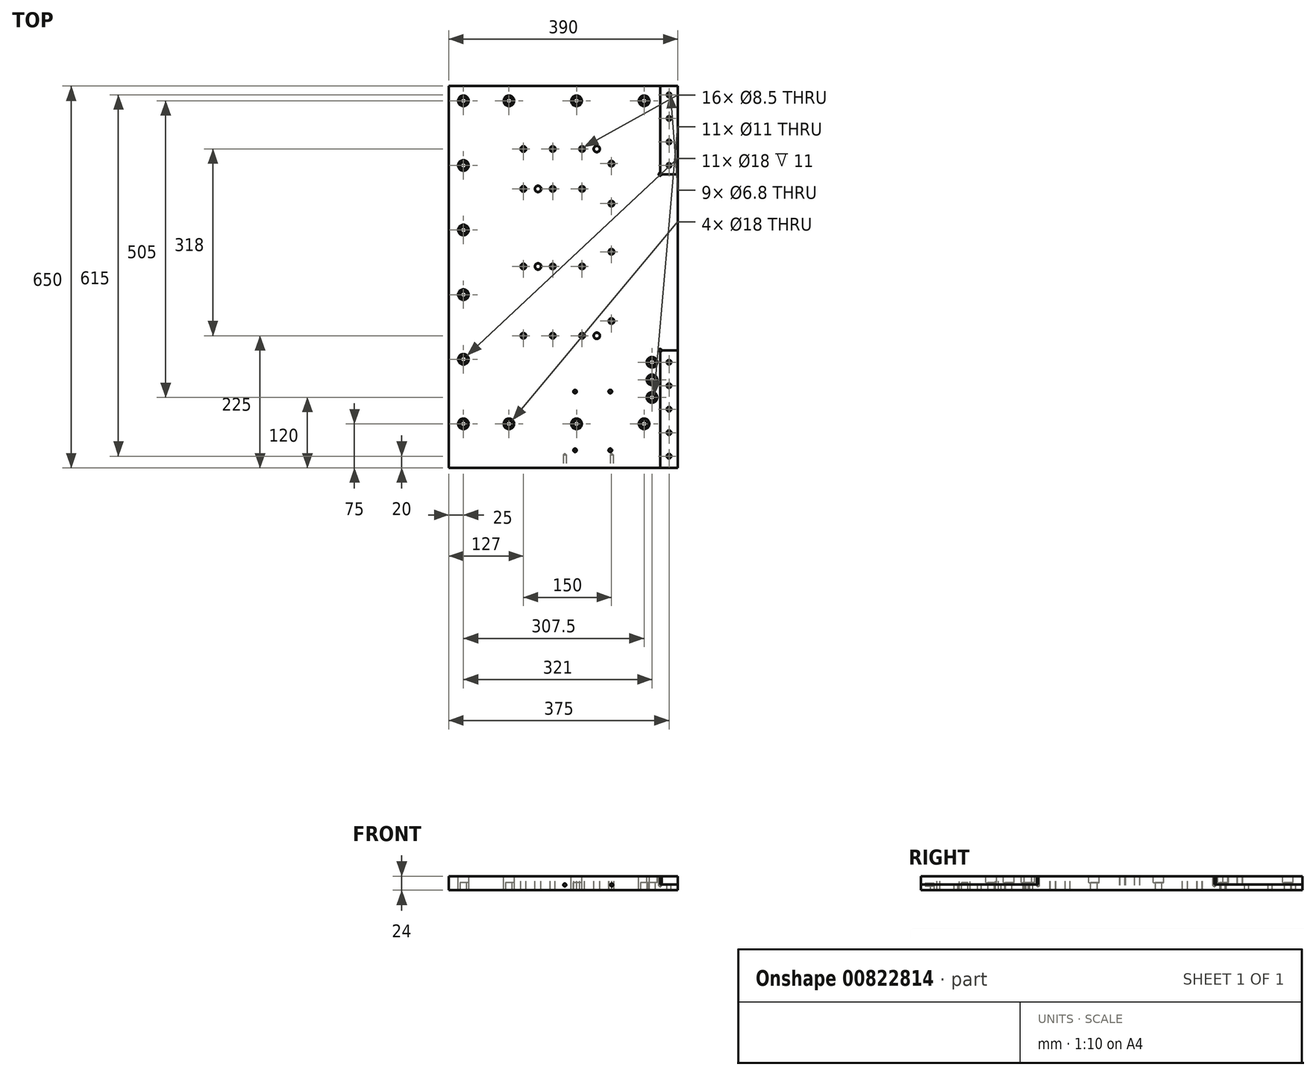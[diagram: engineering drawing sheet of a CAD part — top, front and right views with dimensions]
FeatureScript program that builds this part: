
annotation { "Feature Type Name" : "Feature", "Feature Type Description" : "" }
export const myFeature = defineFeature(function(context is Context, id is Id, definition is map)
    precondition{}
    {
        {
            var Q0;
            Q0=qCreatedBy(makeId("Top.planeOp"),FACE);
            var sketch = newSketch(context, id + "F0", { "sketchPlane" : qUnion([Q0])});
            skLineSegment(sketch, "E0.bottom", {"start": v(-195, -325) * mm, "end": v(195, -325) * mm});
            skLineSegment(sketch, "E0.top", {"start": v(-195, 325) * mm, "end": v(195, 325) * mm});
            skLineSegment(sketch, "E0.left", {"start": v(-195, -325) * mm, "end": v(-195, 325) * mm});
            skLineSegment(sketch, "E0.right", {"start": v(195, -325) * mm, "end": v(195, 325) * mm});
            skPoint(sketch, "E0.middle", {"position": v(0, 0) * mm});
            skSolve(sketch);
        }
        {
            var Q0;
            Q0 = qSketchRegion(id + "F0", true);
            extrude(context, id + "F1", {"entities" : qUnion([Q0]), "depth" : 24 * mm, "offsetDistance" : 25 * mm});
        }
        {
            var Q0;
            Q0=makeQuery(id+"F1.opExtrude","CAP_FACE",FACE,{"disambiguationData":[OSD([sQuery(id+"F0.wireOp",EDGE,"E0.bottom"),sQuery(id+"F0.wireOp",EDGE,"E0.top"),sQuery(id+"F0.wireOp",EDGE,"E0.left"),sQuery(id+"F0.wireOp",EDGE,"E0.right")])],"isStart":false});
            var sketch = newSketch(context, id + "F2", { "sketchPlane" : qUnion([Q0])});
            skLineSegment(sketch, "E1.0.0", {"start": v(195, 325) * mm, "end": v(-195, 325) * mm, "construction": true});
            skLineSegment(sketch, "E1.0.1", {"start": v(-195, 325) * mm, "end": v(-195, -325) * mm, "construction": true});
            skLineSegment(sketch, "E1.0.2", {"start": v(-195, -325) * mm, "end": v(195, -325) * mm, "construction": true});
            skLineSegment(sketch, "E1.0.3", {"start": v(195, -325) * mm, "end": v(195, 325) * mm, "construction": true});
            skLineSegment(sketch, "E2", {"start": v(195, -125) * mm, "end": v(165, -125) * mm, "construction": true});
            skLineSegment(sketch, "E3", {"start": v(165, -125) * mm, "end": v(165, -325) * mm, "construction": true});
            skLineSegment(sketch, "E4", {"start": v(195, 175) * mm, "end": v(165, 175) * mm, "construction": true});
            skLineSegment(sketch, "E5", {"start": v(165, 175) * mm, "end": v(165, 325) * mm, "construction": true});
            skLineSegment(sketch, "E6.bottom", {"start": v(165, 175) * mm, "end": v(195, 175) * mm});
            skLineSegment(sketch, "E6.top", {"start": v(165, 325) * mm, "end": v(195, 325) * mm});
            skLineSegment(sketch, "E6.left", {"start": v(165, 175) * mm, "end": v(165, 325) * mm});
            skLineSegment(sketch, "E6.right", {"start": v(195, 175) * mm, "end": v(195, 325) * mm});
            skLineSegment(sketch, "E7.bottom", {"start": v(165, -125) * mm, "end": v(195, -125) * mm});
            skLineSegment(sketch, "E7.top", {"start": v(165, -325) * mm, "end": v(195, -325) * mm});
            skLineSegment(sketch, "E7.left", {"start": v(165, -125) * mm, "end": v(165, -325) * mm});
            skLineSegment(sketch, "E7.right", {"start": v(195, -125) * mm, "end": v(195, -325) * mm});
            skSolve(sketch);
        }
        {
            var Q0;
            {var subQ3=sQuery(id+"F2.wireOp",EDGE,"E6.bottom");Q0=makeQuery(id+"F2.imprint","IMPRINT",FACE,{"disambiguationData":[TD([[makeQuery(id+"F2.imprint","IMPRINT",EDGE,{"derivedFrom":subQ3}),-1.0]])]});}
            var sketch = newSketch(context, id + "F3", { "sketchPlane" : qUnion([Q0])});
            skLineSegment(sketch, "E8.0", {"start": v(165, 175) * mm, "end": v(165, 325) * mm, "construction": true});
            skLineSegment(sketch, "E9.0", {"start": v(165, 175) * mm, "end": v(195, 175) * mm, "construction": true});
            skLineSegment(sketch, "E10.0", {"start": v(165, -125) * mm, "end": v(195, -125) * mm, "construction": true});
            skLineSegment(sketch, "E11.0", {"start": v(165, -125) * mm, "end": v(165, -325) * mm, "construction": true});
            skCircle(sketch, "E12", {"center": v(165, 175) * mm, "radius": 2.5 * mm});
            skCircle(sketch, "E13", {"center": v(165, -125) * mm, "radius": 2.5 * mm});
            skSolve(sketch);
        }
        {
            var Q0;
            Q0 = qSketchRegion(id + "F2", true);
            extrude(context, id + "F4", {"entities" : qUnion([Q0]), "operationType" : NewBodyOperationType.REMOVE, "oppositeDirection" : true, "depth" : 14 * mm, "offsetDistance" : 25 * mm});
        }
        {
            var Q0;
            Q0 = qSketchRegion(id + "F3", true);
            extrude(context, id + "F5", {"entities" : qUnion([Q0]), "operationType" : NewBodyOperationType.REMOVE, "oppositeDirection" : true, "depth" : (16 + 2.5) * mm, "offsetDistance" : 25 * mm});
        }
        {
            var Q0;
            Q0=makeQuery(id+"F5.boolean.opBoolean","COPY",FACE,{"derivedFrom":makeQuery(id+"F5.opExtrude","CAP_FACE",FACE,{"disambiguationData":[OSD([sQuery(id+"F3.wireOp",EDGE,"E13")])],"isStart":false})});
            var Q1;
            Q1=makeQuery(id+"F5.boolean.opBoolean","COPY",FACE,{"derivedFrom":makeQuery(id+"F5.opExtrude","CAP_FACE",FACE,{"disambiguationData":[OSD([sQuery(id+"F3.wireOp",EDGE,"E12")])],"isStart":false})});
            chamfer(context, id + "F6", {"entities" : qUnion([Q0, Q1]), "width" : 2.5 * mm, "tangentPropagation" : true});
        }
        {
            var Q0;
            Q0=makeQuery(id+"F1.opExtrude","CAP_FACE",FACE,{"disambiguationData":[OSD([sQuery(id+"F0.wireOp",EDGE,"E0.bottom"),sQuery(id+"F0.wireOp",EDGE,"E0.top"),sQuery(id+"F0.wireOp",EDGE,"E0.left"),sQuery(id+"F0.wireOp",EDGE,"E0.right")])],"isStart":false});
            var sketch = newSketch(context, id + "F7", { "sketchPlane" : qUnion([Q0])});
            skLineSegment(sketch, "E14.bottom", {"start": v(479.08, -265.8) * mm, "end": v(-298.76, -265.8) * mm, "construction": true});
            skLineSegment(sketch, "E14.top", {"start": v(479.08, -215) * mm, "end": v(-298.76, -215) * mm, "construction": true});
            skLineSegment(sketch, "E14.left", {"start": v(479.08, -265.8) * mm, "end": v(479.08, -215) * mm, "construction": true});
            skLineSegment(sketch, "E14.right", {"start": v(-298.76, -265.8) * mm, "end": v(-298.76, -215) * mm, "construction": true});
            skLineSegment(sketch, "E15.bottom", {"start": v(-285.1, 315.8) * mm, "end": v(454.5, 315.8) * mm, "construction": true});
            skLineSegment(sketch, "E15.top", {"start": v(-285.1, 265) * mm, "end": v(454.5, 265) * mm, "construction": true});
            skLineSegment(sketch, "E15.left", {"start": v(-285.1, 315.8) * mm, "end": v(-285.1, 265) * mm, "construction": true});
            skLineSegment(sketch, "E15.right", {"start": v(454.5, 315.8) * mm, "end": v(454.5, 265) * mm, "construction": true});
            skArc(sketch, "E16.0.0", {"start": v(167.5, 175) * mm, "mid": v(163.23, 173.23) * mm, "end": v(165, 177.5) * mm, "construction": true});
            skLineSegment(sketch, "E16.0.1", {"start": v(165, 177.5) * mm, "end": v(165, 325) * mm, "construction": true});
            skLineSegment(sketch, "E16.0.2", {"start": v(165, 325) * mm, "end": v(-195, 325) * mm, "construction": true});
            skLineSegment(sketch, "E16.0.3", {"start": v(-195, 325) * mm, "end": v(-195, -325) * mm, "construction": true});
            skLineSegment(sketch, "E16.0.4", {"start": v(-195, -325) * mm, "end": v(165, -325) * mm, "construction": true});
            skLineSegment(sketch, "E16.0.5", {"start": v(165, -325) * mm, "end": v(165, -127.5) * mm, "construction": true});
            skArc(sketch, "E16.0.6", {"start": v(165, -127.5) * mm, "mid": v(163.23, -123.23) * mm, "end": v(167.5, -125) * mm, "construction": true});
            skLineSegment(sketch, "E16.0.7", {"start": v(167.5, -125) * mm, "end": v(195, -125) * mm, "construction": true});
            skLineSegment(sketch, "E16.0.8", {"start": v(195, -125) * mm, "end": v(195, 175) * mm, "construction": true});
            skLineSegment(sketch, "E16.0.9", {"start": v(195, 175) * mm, "end": v(167.5, 175) * mm, "construction": true});
            skArc(sketch, "E17.0.0", {"start": v(165, 202.5) * mm, "mid": v(192.5, 202.5) * mm, "end": v(192.5, 175) * mm, "construction": true});
            skLineSegment(sketch, "E17.0.1", {"start": v(192.5, 175) * mm, "end": v(195, 175) * mm, "construction": true});
            skLineSegment(sketch, "E17.0.2", {"start": v(195, 175) * mm, "end": v(195, 325) * mm, "construction": true});
            skLineSegment(sketch, "E17.0.3", {"start": v(195, 325) * mm, "end": v(165, 325) * mm, "construction": true});
            skLineSegment(sketch, "E17.0.4", {"start": v(165, 325) * mm, "end": v(165, 202.5) * mm, "construction": true});
            skArc(sketch, "E18.0.0", {"start": v(192.5, -125) * mm, "mid": v(167.5, -127.5) * mm, "end": v(165, -102.5) * mm, "construction": true});
            skLineSegment(sketch, "E18.0.1", {"start": v(165, -102.5) * mm, "end": v(165, -325) * mm, "construction": true});
            skLineSegment(sketch, "E18.0.2", {"start": v(165, -325) * mm, "end": v(195, -325) * mm, "construction": true});
            skLineSegment(sketch, "E18.0.3", {"start": v(195, -325) * mm, "end": v(195, -125) * mm, "construction": true});
            skLineSegment(sketch, "E18.0.4", {"start": v(195, -125) * mm, "end": v(192.5, -125) * mm, "construction": true});
            skPoint(sketch, "E19.endSnap0", {"position": v(181.25, 175) * mm});
            skLineSegment(sketch, "E20", {"start": v(180, -325) * mm, "end": v(180, 325) * mm, "construction": true});
            skCircle(sketch, "E21", {"center": v(180, 310) * mm, "radius": 3.4 * mm});
            skCircle(sketch, "E22", {"center": v(180, 230) * mm, "radius": 3.4 * mm});
            skCircle(sketch, "E23", {"center": v(180, 190) * mm, "radius": 3.4 * mm});
            skCircle(sketch, "E24", {"center": v(180, -145) * mm, "radius": 3.4 * mm});
            skCircle(sketch, "E25", {"center": v(180, -185) * mm, "radius": 3.4 * mm});
            skCircle(sketch, "E26", {"center": v(180, -225) * mm, "radius": 3.4 * mm});
            skCircle(sketch, "E27", {"center": v(180, -265) * mm, "radius": 3.4 * mm});
            skCircle(sketch, "E28", {"center": v(180, -305) * mm, "radius": 3.4 * mm});
            skCircle(sketch, "E29", {"center": v(180, 270) * mm, "radius": 3.4 * mm});
            skCircle(sketch, "E30", {"center": v(180, -345) * mm, "radius": 3.4 * mm, "construction": true});
            skSolve(sketch);
        }
        {
            var Q0;
            Q0 = qSketchRegion(id + "F7", true);
            extrude(context, id + "F8", {"entities" : qUnion([Q0]), "operationType" : NewBodyOperationType.REMOVE, "oppositeDirection" : true, "depth" : 25 * mm, "offsetDistance" : 25 * mm});
        }
        {
            var Q0;
            Q0=makeQuery(id+"F8.boolean.opBoolean","COPY",FACE,{"derivedFrom":makeQuery(id+"F8.opExtrude","SWEPT_FACE",FACE,{"disambiguationData":[OSD([sQuery(id+"F7.wireOp",EDGE,"E28")])]})});
            var Q1;
            Q1=makeQuery(id+"F8.boolean.opBoolean","COPY",FACE,{"derivedFrom":makeQuery(id+"F8.opExtrude","SWEPT_FACE",FACE,{"disambiguationData":[OSD([sQuery(id+"F7.wireOp",EDGE,"E27")])]})});
            var Q2;
            Q2=makeQuery(id+"F8.boolean.opBoolean","COPY",FACE,{"derivedFrom":makeQuery(id+"F8.opExtrude","SWEPT_FACE",FACE,{"disambiguationData":[OSD([sQuery(id+"F7.wireOp",EDGE,"E26")])]})});
            var Q3;
            Q3=makeQuery(id+"F8.boolean.opBoolean","COPY",FACE,{"derivedFrom":makeQuery(id+"F8.opExtrude","SWEPT_FACE",FACE,{"disambiguationData":[OSD([sQuery(id+"F7.wireOp",EDGE,"E25")])]})});
            var Q4;
            Q4=makeQuery(id+"F8.boolean.opBoolean","COPY",FACE,{"derivedFrom":makeQuery(id+"F8.opExtrude","SWEPT_FACE",FACE,{"disambiguationData":[OSD([sQuery(id+"F7.wireOp",EDGE,"E24")])]})});
            var Q5;
            Q5=makeQuery(id+"F8.boolean.opBoolean","COPY",FACE,{"derivedFrom":makeQuery(id+"F8.opExtrude","SWEPT_FACE",FACE,{"disambiguationData":[OSD([sQuery(id+"F7.wireOp",EDGE,"E23")])]})});
            var Q6;
            Q6=makeQuery(id+"F8.boolean.opBoolean","COPY",FACE,{"derivedFrom":makeQuery(id+"F8.opExtrude","SWEPT_FACE",FACE,{"disambiguationData":[OSD([sQuery(id+"F7.wireOp",EDGE,"E22")])]})});
            var Q7;
            Q7=makeQuery(id+"F8.boolean.opBoolean","COPY",FACE,{"derivedFrom":makeQuery(id+"F8.opExtrude","SWEPT_FACE",FACE,{"disambiguationData":[OSD([sQuery(id+"F7.wireOp",EDGE,"E29")])]})});
            var Q8;
            Q8=makeQuery(id+"F8.boolean.opBoolean","COPY",FACE,{"derivedFrom":makeQuery(id+"F8.opExtrude","SWEPT_FACE",FACE,{"disambiguationData":[OSD([sQuery(id+"F7.wireOp",EDGE,"E21")])]})});
            chamfer(context, id + "F9", {"entities" : qUnion([Q0, Q1, Q2, Q3, Q4, Q5, Q6, Q7, Q8]), "width" : 0.5 * mm, "tangentPropagation" : true});
        }
        {
            var Q0;
            Q0=makeQuery(id+"F1.opExtrude","CAP_FACE",FACE,{"disambiguationData":[OSD([sQuery(id+"F0.wireOp",EDGE,"E0.bottom"),sQuery(id+"F0.wireOp",EDGE,"E0.top"),sQuery(id+"F0.wireOp",EDGE,"E0.left"),sQuery(id+"F0.wireOp",EDGE,"E0.right")])],"isStart":false});
            var sketch = newSketch(context, id + "F10", { "sketchPlane" : qUnion([Q0])});
            skLineSegment(sketch, "E31.0", {"start": v(-195, -325) * mm, "end": v(-195, 325) * mm, "construction": true});
            skLineSegment(sketch, "E32.0", {"start": v(-195, 325) * mm, "end": v(165, 325) * mm, "construction": true});
            skLineSegment(sketch, "E33.0", {"start": v(195, -125) * mm, "end": v(195, 175) * mm, "construction": true});
            skLineSegment(sketch, "E34", {"start": v(-353.17, 300) * mm, "end": v(198.25, 300) * mm, "construction": true});
            skCircle(sketch, "E35", {"center": v(137.5, 300) * mm, "radius": 5.5 * mm});
            skCircle(sketch, "E36.1.0.0", {"center": v(22.5, 300) * mm, "radius": 5.5 * mm});
            skCircle(sketch, "E36.2.0.0", {"center": v(-92.5, 300) * mm, "radius": 5.5 * mm});
            skLineSegment(sketch, "E36.direction1", {"start": v(137.5, 300) * mm, "end": v(22.5, 300) * mm, "construction": true});
            skCircle(sketch, "E37.0.3.0", {"center": v(-207.5, 300) * mm, "radius": 5.5 * mm, "construction": true});
            skLineSegment(sketch, "E38", {"start": v(-117.5, 418.15) * mm, "end": v(-117.5, -388.99) * mm, "construction": true});
            skLineSegment(sketch, "E39", {"start": v(-67.5, 418.15) * mm, "end": v(-67.5, -388.99) * mm, "construction": true});
            skLineSegment(sketch, "E40", {"start": v(195, 25) * mm, "end": v(452.46, 25) * mm, "construction": true});
            skCircle(sketch, "E41.MirrorC", {"center": v(22.5, -250) * mm, "radius": 5.5 * mm});
            skCircle(sketch, "E42.MirrorC", {"center": v(137.5, -250) * mm, "radius": 5.5 * mm});
            skCircle(sketch, "E43.MirrorC", {"center": v(-92.5, -250) * mm, "radius": 5.5 * mm});
            skCircle(sketch, "E44", {"center": v(-170, 300) * mm, "radius": 5.5 * mm});
            skCircle(sketch, "E45.MirrorC", {"center": v(-170, -250) * mm, "radius": 5.5 * mm});
            skCircle(sketch, "E46.0.1.0", {"center": v(-170, 190) * mm, "radius": 5.5 * mm});
            skCircle(sketch, "E46.0.2.0", {"center": v(-170, 80) * mm, "radius": 5.5 * mm});
            skCircle(sketch, "E46.0.3.0", {"center": v(-170, -30) * mm, "radius": 5.5 * mm});
            skCircle(sketch, "E46.0.4.0", {"center": v(-170, -140) * mm, "radius": 5.5 * mm});
            skLineSegment(sketch, "E46.direction1", {"start": v(-170, 300) * mm, "end": v(-145, 300) * mm, "construction": true});
            skLineSegment(sketch, "E46.direction2", {"start": v(-170, 300) * mm, "end": v(-170, 190) * mm, "construction": true});
            skCircle(sketch, "E47", {"center": v(-170, 300) * mm, "radius": 9 * mm});
            skCircle(sketch, "E48", {"center": v(-92.5, 300) * mm, "radius": 9 * mm});
            skCircle(sketch, "E49.0.1.0", {"center": v(-170, 190) * mm, "radius": 9 * mm});
            skCircle(sketch, "E49.0.2.0", {"center": v(-170, 80) * mm, "radius": 9 * mm});
            skCircle(sketch, "E49.0.3.0", {"center": v(-170, -30) * mm, "radius": 9 * mm});
            skCircle(sketch, "E49.0.4.0", {"center": v(-170, -140) * mm, "radius": 9 * mm});
            skCircle(sketch, "E49.0.5.0", {"center": v(-170, -250) * mm, "radius": 9 * mm});
            skCircle(sketch, "E50.1.0.0", {"center": v(22.5, 300) * mm, "radius": 9 * mm});
            skCircle(sketch, "E50.2.0.0", {"center": v(137.5, 300) * mm, "radius": 9 * mm});
            skLineSegment(sketch, "E50.direction1", {"start": v(-92.5, 300) * mm, "end": v(22.5, 300) * mm, "construction": true});
            skCircle(sketch, "E51.MirrorC", {"center": v(22.5, -250) * mm, "radius": 9 * mm});
            skCircle(sketch, "E52.MirrorC", {"center": v(137.5, -250) * mm, "radius": 9 * mm});
            skCircle(sketch, "E53.MirrorC", {"center": v(-92.5, -250) * mm, "radius": 9 * mm});
            skSolve(sketch);
        }
        {
            var Q0;
            Q0=makeQuery(id+"F10.imprint","IMPRINT",FACE,{"disambiguationData":[TD([[makeQuery(id+"F10.imprint","IMPRINT",EDGE,{"derivedFrom":sQuery(id+"F10.wireOp",EDGE,"E35")}),1.0]])]});
            var Q1;
            Q1=makeQuery(id+"F10.imprint","IMPRINT",FACE,{"disambiguationData":[TD([[makeQuery(id+"F10.imprint","IMPRINT",EDGE,{"derivedFrom":sQuery(id+"F10.wireOp",EDGE,"E36.1.0.0")}),1.0]])]});
            var Q2;
            Q2=makeQuery(id+"F10.imprint","IMPRINT",FACE,{"disambiguationData":[TD([[makeQuery(id+"F10.imprint","IMPRINT",EDGE,{"derivedFrom":sQuery(id+"F10.wireOp",EDGE,"E36.2.0.0")}),1.0]])]});
            var Q3;
            Q3=makeQuery(id+"F10.imprint","IMPRINT",FACE,{"disambiguationData":[TD([[makeQuery(id+"F10.imprint","IMPRINT",EDGE,{"derivedFrom":sQuery(id+"F10.wireOp",EDGE,"E44")}),1.0]])]});
            var Q4;
            Q4=makeQuery(id+"F10.imprint","IMPRINT",FACE,{"disambiguationData":[TD([[makeQuery(id+"F10.imprint","IMPRINT",EDGE,{"derivedFrom":sQuery(id+"F10.wireOp",EDGE,"E46.0.1.0")}),1.0]])]});
            var Q5;
            Q5=makeQuery(id+"F10.imprint","IMPRINT",FACE,{"disambiguationData":[TD([[makeQuery(id+"F10.imprint","IMPRINT",EDGE,{"derivedFrom":sQuery(id+"F10.wireOp",EDGE,"E46.0.2.0")}),1.0]])]});
            var Q6;
            Q6=makeQuery(id+"F10.imprint","IMPRINT",FACE,{"disambiguationData":[TD([[makeQuery(id+"F10.imprint","IMPRINT",EDGE,{"derivedFrom":sQuery(id+"F10.wireOp",EDGE,"E46.0.3.0")}),1.0]])]});
            var Q7;
            Q7=makeQuery(id+"F10.imprint","IMPRINT",FACE,{"disambiguationData":[TD([[makeQuery(id+"F10.imprint","IMPRINT",EDGE,{"derivedFrom":sQuery(id+"F10.wireOp",EDGE,"E46.0.4.0")}),1.0]])]});
            var Q8;
            Q8=makeQuery(id+"F10.imprint","IMPRINT",FACE,{"disambiguationData":[TD([[makeQuery(id+"F10.imprint","IMPRINT",EDGE,{"derivedFrom":sQuery(id+"F10.wireOp",EDGE,"E45.MirrorC")}),-1.0]])]});
            var Q9;
            Q9=makeQuery(id+"F10.imprint","IMPRINT",FACE,{"disambiguationData":[TD([[makeQuery(id+"F10.imprint","IMPRINT",EDGE,{"derivedFrom":sQuery(id+"F10.wireOp",EDGE,"E43.MirrorC")}),-1.0]])]});
            var Q10;
            Q10=makeQuery(id+"F10.imprint","IMPRINT",FACE,{"disambiguationData":[TD([[makeQuery(id+"F10.imprint","IMPRINT",EDGE,{"derivedFrom":sQuery(id+"F10.wireOp",EDGE,"E41.MirrorC")}),-1.0]])]});
            var Q11;
            Q11=makeQuery(id+"F10.imprint","IMPRINT",FACE,{"disambiguationData":[TD([[makeQuery(id+"F10.imprint","IMPRINT",EDGE,{"derivedFrom":sQuery(id+"F10.wireOp",EDGE,"E42.MirrorC")}),-1.0]])]});
            extrude(context, id + "F11", {"entities" : qUnion([Q0, Q1, Q2, Q3, Q4, Q5, Q6, Q7, Q8, Q9, Q10, Q11]), "operationType" : NewBodyOperationType.REMOVE, "oppositeDirection" : true, "depth" : 25 * mm, "offsetDistance" : 25 * mm});
        }
        {
            var Q0;
            Q0=makeQuery(id+"F10.imprint","IMPRINT",FACE,{"disambiguationData":[TD([[makeQuery(id+"F10.imprint","IMPRINT",EDGE,{"derivedFrom":sQuery(id+"F10.wireOp",EDGE,"E35")}),-1.0]])]});
            var Q1;
            Q1=makeQuery(id+"F10.imprint","IMPRINT",FACE,{"disambiguationData":[TD([[makeQuery(id+"F10.imprint","IMPRINT",EDGE,{"derivedFrom":sQuery(id+"F10.wireOp",EDGE,"E36.1.0.0")}),-1.0]])]});
            var Q2;
            Q2=makeQuery(id+"F10.imprint","IMPRINT",FACE,{"disambiguationData":[TD([[makeQuery(id+"F10.imprint","IMPRINT",EDGE,{"derivedFrom":sQuery(id+"F10.wireOp",EDGE,"E36.2.0.0")}),-1.0]])]});
            var Q3;
            Q3=makeQuery(id+"F10.imprint","IMPRINT",FACE,{"disambiguationData":[TD([[makeQuery(id+"F10.imprint","IMPRINT",EDGE,{"derivedFrom":sQuery(id+"F10.wireOp",EDGE,"E44")}),-1.0]])]});
            var Q4;
            Q4=makeQuery(id+"F10.imprint","IMPRINT",FACE,{"disambiguationData":[TD([[makeQuery(id+"F10.imprint","IMPRINT",EDGE,{"derivedFrom":sQuery(id+"F10.wireOp",EDGE,"E46.0.1.0")}),-1.0]])]});
            var Q5;
            Q5=makeQuery(id+"F10.imprint","IMPRINT",FACE,{"disambiguationData":[TD([[makeQuery(id+"F10.imprint","IMPRINT",EDGE,{"derivedFrom":sQuery(id+"F10.wireOp",EDGE,"E46.0.2.0")}),-1.0]])]});
            var Q6;
            Q6=makeQuery(id+"F10.imprint","IMPRINT",FACE,{"disambiguationData":[TD([[makeQuery(id+"F10.imprint","IMPRINT",EDGE,{"derivedFrom":sQuery(id+"F10.wireOp",EDGE,"E46.0.3.0")}),-1.0]])]});
            var Q7;
            Q7=makeQuery(id+"F10.imprint","IMPRINT",FACE,{"disambiguationData":[TD([[makeQuery(id+"F10.imprint","IMPRINT",EDGE,{"derivedFrom":sQuery(id+"F10.wireOp",EDGE,"E46.0.4.0")}),-1.0]])]});
            var Q8;
            Q8=makeQuery(id+"F10.imprint","IMPRINT",FACE,{"disambiguationData":[TD([[makeQuery(id+"F10.imprint","IMPRINT",EDGE,{"derivedFrom":sQuery(id+"F10.wireOp",EDGE,"E45.MirrorC")}),1.0]])]});
            var Q9;
            Q9=makeQuery(id+"F10.imprint","IMPRINT",FACE,{"disambiguationData":[TD([[makeQuery(id+"F10.imprint","IMPRINT",EDGE,{"derivedFrom":sQuery(id+"F10.wireOp",EDGE,"E43.MirrorC")}),1.0]])]});
            var Q10;
            Q10=makeQuery(id+"F10.imprint","IMPRINT",FACE,{"disambiguationData":[TD([[makeQuery(id+"F10.imprint","IMPRINT",EDGE,{"derivedFrom":sQuery(id+"F10.wireOp",EDGE,"E41.MirrorC")}),1.0]])]});
            var Q11;
            Q11=makeQuery(id+"F10.imprint","IMPRINT",FACE,{"disambiguationData":[TD([[makeQuery(id+"F10.imprint","IMPRINT",EDGE,{"derivedFrom":sQuery(id+"F10.wireOp",EDGE,"E42.MirrorC")}),1.0]])]});
            extrude(context, id + "F12", {"entities" : qUnion([Q0, Q1, Q2, Q3, Q4, Q5, Q6, Q7, Q8, Q9, Q10, Q11]), "operationType" : NewBodyOperationType.REMOVE, "oppositeDirection" : true, "depth" : 11 * mm, "offsetDistance" : 25 * mm});
        }
        {
            var Q0;
            Q0=makeQuery(id+"F12.boolean.opBoolean","COPY",EDGE,{"derivedFrom":makeQuery(id+"F12.opExtrude","CAP_EDGE",EDGE,{"disambiguationData":[OSD([sQuery(id+"F10.wireOp",EDGE,"E47")])],"isStart":true})});
            var Q1;
            Q1=makeQuery(id+"F12.boolean.opBoolean","COPY",EDGE,{"derivedFrom":makeQuery(id+"F12.opExtrude","CAP_EDGE",EDGE,{"disambiguationData":[OSD([sQuery(id+"F10.wireOp",EDGE,"E50.1.0.0")])],"isStart":true})});
            var Q2;
            Q2=makeQuery(id+"F12.boolean.opBoolean","COPY",EDGE,{"derivedFrom":makeQuery(id+"F12.opExtrude","CAP_EDGE",EDGE,{"disambiguationData":[OSD([sQuery(id+"F10.wireOp",EDGE,"E50.2.0.0")])],"isStart":true})});
            var Q3;
            Q3=makeQuery(id+"F12.boolean.opBoolean","COPY",EDGE,{"derivedFrom":makeQuery(id+"F12.opExtrude","CAP_EDGE",EDGE,{"disambiguationData":[OSD([sQuery(id+"F10.wireOp",EDGE,"E48")])],"isStart":true})});
            var Q4;
            Q4=makeQuery(id+"F12.boolean.opBoolean","COPY",EDGE,{"derivedFrom":makeQuery(id+"F12.opExtrude","CAP_EDGE",EDGE,{"disambiguationData":[OSD([sQuery(id+"F10.wireOp",EDGE,"E49.0.1.0")])],"isStart":true})});
            var Q5;
            Q5=makeQuery(id+"F12.boolean.opBoolean","COPY",EDGE,{"derivedFrom":makeQuery(id+"F12.opExtrude","CAP_EDGE",EDGE,{"disambiguationData":[OSD([sQuery(id+"F10.wireOp",EDGE,"E49.0.2.0")])],"isStart":true})});
            var Q6;
            Q6=makeQuery(id+"F12.boolean.opBoolean","COPY",EDGE,{"derivedFrom":makeQuery(id+"F12.opExtrude","CAP_EDGE",EDGE,{"disambiguationData":[OSD([sQuery(id+"F10.wireOp",EDGE,"E52.MirrorC")])],"isStart":true})});
            var Q7;
            Q7=makeQuery(id+"F12.boolean.opBoolean","COPY",EDGE,{"derivedFrom":makeQuery(id+"F12.opExtrude","CAP_EDGE",EDGE,{"disambiguationData":[OSD([sQuery(id+"F10.wireOp",EDGE,"E51.MirrorC")])],"isStart":true})});
            var Q8;
            Q8=makeQuery(id+"F12.boolean.opBoolean","COPY",EDGE,{"derivedFrom":makeQuery(id+"F12.opExtrude","CAP_EDGE",EDGE,{"disambiguationData":[OSD([sQuery(id+"F10.wireOp",EDGE,"E49.0.3.0")])],"isStart":true})});
            var Q9;
            Q9=makeQuery(id+"F12.boolean.opBoolean","COPY",EDGE,{"derivedFrom":makeQuery(id+"F12.opExtrude","CAP_EDGE",EDGE,{"disambiguationData":[OSD([sQuery(id+"F10.wireOp",EDGE,"E49.0.4.0")])],"isStart":true})});
            var Q10;
            Q10=makeQuery(id+"F12.boolean.opBoolean","COPY",EDGE,{"derivedFrom":makeQuery(id+"F12.opExtrude","CAP_EDGE",EDGE,{"disambiguationData":[OSD([sQuery(id+"F10.wireOp",EDGE,"E49.0.5.0")])],"isStart":true})});
            var Q11;
            Q11=makeQuery(id+"F12.boolean.opBoolean","COPY",EDGE,{"derivedFrom":makeQuery(id+"F12.opExtrude","CAP_EDGE",EDGE,{"disambiguationData":[OSD([sQuery(id+"F10.wireOp",EDGE,"E53.MirrorC")])],"isStart":true})});
            var Q12;
            Q12=makeQuery(id+"F11.boolean.opBoolean","INTERSECT",EDGE,{"derivedFrom":[makeQuery(id+"F1.opExtrude","CAP_FACE",FACE,{"disambiguationData":[OSD([sQuery(id+"F0.wireOp",EDGE,"E0.bottom"),sQuery(id+"F0.wireOp",EDGE,"E0.top"),sQuery(id+"F0.wireOp",EDGE,"E0.left"),sQuery(id+"F0.wireOp",EDGE,"E0.right")])],"isStart":true}),makeQuery(id+"F11.opExtrude","SWEPT_FACE",FACE,{"disambiguationData":[OSD([sQuery(id+"F10.wireOp",EDGE,"E42.MirrorC")])]})]});
            var Q13;
            Q13=makeQuery(id+"F11.boolean.opBoolean","INTERSECT",EDGE,{"derivedFrom":[makeQuery(id+"F1.opExtrude","CAP_FACE",FACE,{"disambiguationData":[OSD([sQuery(id+"F0.wireOp",EDGE,"E0.bottom"),sQuery(id+"F0.wireOp",EDGE,"E0.top"),sQuery(id+"F0.wireOp",EDGE,"E0.left"),sQuery(id+"F0.wireOp",EDGE,"E0.right")])],"isStart":true}),makeQuery(id+"F11.opExtrude","SWEPT_FACE",FACE,{"disambiguationData":[OSD([sQuery(id+"F10.wireOp",EDGE,"E41.MirrorC")])]})]});
            var Q14;
            Q14=makeQuery(id+"F11.boolean.opBoolean","INTERSECT",EDGE,{"derivedFrom":[makeQuery(id+"F1.opExtrude","CAP_FACE",FACE,{"disambiguationData":[OSD([sQuery(id+"F0.wireOp",EDGE,"E0.bottom"),sQuery(id+"F0.wireOp",EDGE,"E0.top"),sQuery(id+"F0.wireOp",EDGE,"E0.left"),sQuery(id+"F0.wireOp",EDGE,"E0.right")])],"isStart":true}),makeQuery(id+"F11.opExtrude","SWEPT_FACE",FACE,{"disambiguationData":[OSD([sQuery(id+"F10.wireOp",EDGE,"E43.MirrorC")])]})]});
            var Q15;
            Q15=makeQuery(id+"F11.boolean.opBoolean","INTERSECT",EDGE,{"derivedFrom":[makeQuery(id+"F1.opExtrude","CAP_FACE",FACE,{"disambiguationData":[OSD([sQuery(id+"F0.wireOp",EDGE,"E0.bottom"),sQuery(id+"F0.wireOp",EDGE,"E0.top"),sQuery(id+"F0.wireOp",EDGE,"E0.left"),sQuery(id+"F0.wireOp",EDGE,"E0.right")])],"isStart":true}),makeQuery(id+"F11.opExtrude","SWEPT_FACE",FACE,{"disambiguationData":[OSD([sQuery(id+"F10.wireOp",EDGE,"E45.MirrorC")])]})]});
            var Q16;
            Q16=makeQuery(id+"F11.boolean.opBoolean","INTERSECT",EDGE,{"derivedFrom":[makeQuery(id+"F1.opExtrude","CAP_FACE",FACE,{"disambiguationData":[OSD([sQuery(id+"F0.wireOp",EDGE,"E0.bottom"),sQuery(id+"F0.wireOp",EDGE,"E0.top"),sQuery(id+"F0.wireOp",EDGE,"E0.left"),sQuery(id+"F0.wireOp",EDGE,"E0.right")])],"isStart":true}),makeQuery(id+"F11.opExtrude","SWEPT_FACE",FACE,{"disambiguationData":[OSD([sQuery(id+"F10.wireOp",EDGE,"E46.0.4.0")])]})]});
            var Q17;
            Q17=makeQuery(id+"F11.boolean.opBoolean","INTERSECT",EDGE,{"derivedFrom":[makeQuery(id+"F1.opExtrude","CAP_FACE",FACE,{"disambiguationData":[OSD([sQuery(id+"F0.wireOp",EDGE,"E0.bottom"),sQuery(id+"F0.wireOp",EDGE,"E0.top"),sQuery(id+"F0.wireOp",EDGE,"E0.left"),sQuery(id+"F0.wireOp",EDGE,"E0.right")])],"isStart":true}),makeQuery(id+"F11.opExtrude","SWEPT_FACE",FACE,{"disambiguationData":[OSD([sQuery(id+"F10.wireOp",EDGE,"E46.0.3.0")])]})]});
            var Q18;
            Q18=makeQuery(id+"F11.boolean.opBoolean","INTERSECT",EDGE,{"derivedFrom":[makeQuery(id+"F1.opExtrude","CAP_FACE",FACE,{"disambiguationData":[OSD([sQuery(id+"F0.wireOp",EDGE,"E0.bottom"),sQuery(id+"F0.wireOp",EDGE,"E0.top"),sQuery(id+"F0.wireOp",EDGE,"E0.left"),sQuery(id+"F0.wireOp",EDGE,"E0.right")])],"isStart":true}),makeQuery(id+"F11.opExtrude","SWEPT_FACE",FACE,{"disambiguationData":[OSD([sQuery(id+"F10.wireOp",EDGE,"E46.0.1.0")])]})]});
            var Q19;
            Q19=makeQuery(id+"F11.boolean.opBoolean","INTERSECT",EDGE,{"derivedFrom":[makeQuery(id+"F1.opExtrude","CAP_FACE",FACE,{"disambiguationData":[OSD([sQuery(id+"F0.wireOp",EDGE,"E0.bottom"),sQuery(id+"F0.wireOp",EDGE,"E0.top"),sQuery(id+"F0.wireOp",EDGE,"E0.left"),sQuery(id+"F0.wireOp",EDGE,"E0.right")])],"isStart":true}),makeQuery(id+"F11.opExtrude","SWEPT_FACE",FACE,{"disambiguationData":[OSD([sQuery(id+"F10.wireOp",EDGE,"E46.0.2.0")])]})]});
            var Q20;
            Q20=makeQuery(id+"F11.boolean.opBoolean","INTERSECT",EDGE,{"derivedFrom":[makeQuery(id+"F1.opExtrude","CAP_FACE",FACE,{"disambiguationData":[OSD([sQuery(id+"F0.wireOp",EDGE,"E0.bottom"),sQuery(id+"F0.wireOp",EDGE,"E0.top"),sQuery(id+"F0.wireOp",EDGE,"E0.left"),sQuery(id+"F0.wireOp",EDGE,"E0.right")])],"isStart":true}),makeQuery(id+"F11.opExtrude","SWEPT_FACE",FACE,{"disambiguationData":[OSD([sQuery(id+"F10.wireOp",EDGE,"E44")])]})]});
            var Q21;
            Q21=makeQuery(id+"F11.boolean.opBoolean","INTERSECT",EDGE,{"derivedFrom":[makeQuery(id+"F1.opExtrude","CAP_FACE",FACE,{"disambiguationData":[OSD([sQuery(id+"F0.wireOp",EDGE,"E0.bottom"),sQuery(id+"F0.wireOp",EDGE,"E0.top"),sQuery(id+"F0.wireOp",EDGE,"E0.left"),sQuery(id+"F0.wireOp",EDGE,"E0.right")])],"isStart":true}),makeQuery(id+"F11.opExtrude","SWEPT_FACE",FACE,{"disambiguationData":[OSD([sQuery(id+"F10.wireOp",EDGE,"E36.2.0.0")])]})]});
            var Q22;
            Q22=makeQuery(id+"F11.boolean.opBoolean","INTERSECT",EDGE,{"derivedFrom":[makeQuery(id+"F1.opExtrude","CAP_FACE",FACE,{"disambiguationData":[OSD([sQuery(id+"F0.wireOp",EDGE,"E0.bottom"),sQuery(id+"F0.wireOp",EDGE,"E0.top"),sQuery(id+"F0.wireOp",EDGE,"E0.left"),sQuery(id+"F0.wireOp",EDGE,"E0.right")])],"isStart":true}),makeQuery(id+"F11.opExtrude","SWEPT_FACE",FACE,{"disambiguationData":[OSD([sQuery(id+"F10.wireOp",EDGE,"E36.1.0.0")])]})]});
            var Q23;
            Q23=makeQuery(id+"F11.boolean.opBoolean","INTERSECT",EDGE,{"derivedFrom":[makeQuery(id+"F1.opExtrude","CAP_FACE",FACE,{"disambiguationData":[OSD([sQuery(id+"F0.wireOp",EDGE,"E0.bottom"),sQuery(id+"F0.wireOp",EDGE,"E0.top"),sQuery(id+"F0.wireOp",EDGE,"E0.left"),sQuery(id+"F0.wireOp",EDGE,"E0.right")])],"isStart":true}),makeQuery(id+"F11.opExtrude","SWEPT_FACE",FACE,{"disambiguationData":[OSD([sQuery(id+"F10.wireOp",EDGE,"E35")])]})]});
            chamfer(context, id + "F13", {"entities" : qUnion([Q0, Q1, Q2, Q3, Q4, Q5, Q6, Q7, Q8, Q9, Q10, Q11, Q12, Q13, Q14, Q15, Q16, Q17, Q18, Q19, Q20, Q21, Q22, Q23]), "width" : 0.5 * mm, "tangentPropagation" : true});
        }
        {
            var Q0;
            Q0=makeQuery(id+"F1.opExtrude","CAP_FACE",FACE,{"disambiguationData":[OSD([sQuery(id+"F0.wireOp",EDGE,"E0.bottom"),sQuery(id+"F0.wireOp",EDGE,"E0.top"),sQuery(id+"F0.wireOp",EDGE,"E0.left"),sQuery(id+"F0.wireOp",EDGE,"E0.right")])],"isStart":false});
            var sketch = newSketch(context, id + "F14", { "sketchPlane" : qUnion([Q0])});
            skLineSegment(sketch, "E54.0", {"start": v(-195, -325) * mm, "end": v(-195, 325) * mm, "construction": true});
            skLineSegment(sketch, "E55.0", {"start": v(195, -125) * mm, "end": v(195, 175) * mm, "construction": true});
            skLineSegment(sketch, "E56", {"start": v(195, 25) * mm, "end": v(-68, 25) * mm, "construction": true});
            skLineSegment(sketch, "E57", {"start": v(-68, 25) * mm, "end": v(-68, 150) * mm, "construction": true});
            skLineSegment(sketch, "E58", {"start": v(-68, 150) * mm, "end": v(82, 150) * mm, "construction": true});
            skLineSegment(sketch, "E59", {"start": v(82, 150) * mm, "end": v(82, 125) * mm, "construction": true});
            skCircle(sketch, "E60", {"center": v(-68, 150) * mm, "radius": 4.25 * mm});
            skCircle(sketch, "E61", {"center": v(-43, 150) * mm, "radius": 5 * mm});
            skCircle(sketch, "E62", {"center": v(82, 125) * mm, "radius": 4.25 * mm});
            skCircle(sketch, "E63.1.0.0", {"center": v(-18, 150) * mm, "radius": 4.25 * mm});
            skCircle(sketch, "E63.2.0.0", {"center": v(32, 150) * mm, "radius": 4.25 * mm});
            skCircle(sketch, "E63.3.0.0", {"center": v(82, 150) * mm, "radius": 4.25 * mm, "construction": true});
            skLineSegment(sketch, "E63.direction1", {"start": v(-68, 150) * mm, "end": v(-18, 150) * mm, "construction": true});
            skCircle(sketch, "E64.MirrorC", {"center": v(-43, -100) * mm, "radius": 5 * mm, "construction": true});
            skCircle(sketch, "E65.MirrorC", {"center": v(82, -75) * mm, "radius": 4.25 * mm});
            skCircle(sketch, "E66.MirrorC", {"center": v(82, -100) * mm, "radius": 4.25 * mm, "construction": true});
            skCircle(sketch, "E67.MirrorC", {"center": v(32, -100) * mm, "radius": 4.25 * mm});
            skCircle(sketch, "E68.MirrorC", {"center": v(-18, -100) * mm, "radius": 4.25 * mm});
            skCircle(sketch, "E69.MirrorC", {"center": v(-68, -100) * mm, "radius": 4.25 * mm});
            skLineSegment(sketch, "E70", {"start": v(7, 150) * mm, "end": v(7, 25) * mm, "construction": true});
            skCircle(sketch, "E71.MirrorC", {"center": v(57, -100) * mm, "radius": 5 * mm});
            skSolve(sketch);
        }
        {
            var Q0;
            Q0 = qSketchRegion(id + "F14", true);
            extrude(context, id + "F15", {"entities" : qUnion([Q0]), "operationType" : NewBodyOperationType.REMOVE, "oppositeDirection" : true, "depth" : 25 * mm, "offsetDistance" : 25 * mm});
        }
        {
            var Q0;
            Q0=makeQuery(id+"F15.boolean.opBoolean","COPY",FACE,{"derivedFrom":makeQuery(id+"F15.opExtrude","SWEPT_FACE",FACE,{"disambiguationData":[OSD([sQuery(id+"F14.wireOp",EDGE,"E65.MirrorC")])]})});
            var Q1;
            Q1=makeQuery(id+"F15.boolean.opBoolean","COPY",FACE,{"derivedFrom":makeQuery(id+"F15.opExtrude","SWEPT_FACE",FACE,{"disambiguationData":[OSD([sQuery(id+"F14.wireOp",EDGE,"E71.MirrorC")])]})});
            var Q2;
            Q2=makeQuery(id+"F15.boolean.opBoolean","COPY",FACE,{"derivedFrom":makeQuery(id+"F15.opExtrude","SWEPT_FACE",FACE,{"disambiguationData":[OSD([sQuery(id+"F14.wireOp",EDGE,"E68.MirrorC")])]})});
            var Q3;
            Q3=makeQuery(id+"F15.boolean.opBoolean","COPY",FACE,{"derivedFrom":makeQuery(id+"F15.opExtrude","SWEPT_FACE",FACE,{"disambiguationData":[OSD([sQuery(id+"F14.wireOp",EDGE,"E67.MirrorC")])]})});
            var Q4;
            Q4=makeQuery(id+"F15.boolean.opBoolean","COPY",FACE,{"derivedFrom":makeQuery(id+"F15.opExtrude","SWEPT_FACE",FACE,{"disambiguationData":[OSD([sQuery(id+"F14.wireOp",EDGE,"E69.MirrorC")])]})});
            var Q5;
            Q5=makeQuery(id+"F15.boolean.opBoolean","COPY",FACE,{"derivedFrom":makeQuery(id+"F15.opExtrude","SWEPT_FACE",FACE,{"disambiguationData":[OSD([sQuery(id+"F14.wireOp",EDGE,"E62")])]})});
            var Q6;
            Q6=makeQuery(id+"F15.boolean.opBoolean","COPY",FACE,{"derivedFrom":makeQuery(id+"F15.opExtrude","SWEPT_FACE",FACE,{"disambiguationData":[OSD([sQuery(id+"F14.wireOp",EDGE,"E63.2.0.0")])]})});
            var Q7;
            Q7=makeQuery(id+"F15.boolean.opBoolean","COPY",FACE,{"derivedFrom":makeQuery(id+"F15.opExtrude","SWEPT_FACE",FACE,{"disambiguationData":[OSD([sQuery(id+"F14.wireOp",EDGE,"E63.1.0.0")])]})});
            var Q8;
            Q8=makeQuery(id+"F15.boolean.opBoolean","COPY",FACE,{"derivedFrom":makeQuery(id+"F15.opExtrude","SWEPT_FACE",FACE,{"disambiguationData":[OSD([sQuery(id+"F14.wireOp",EDGE,"E61")])]})});
            var Q9;
            Q9=makeQuery(id+"F15.boolean.opBoolean","COPY",FACE,{"derivedFrom":makeQuery(id+"F15.opExtrude","SWEPT_FACE",FACE,{"disambiguationData":[OSD([sQuery(id+"F14.wireOp",EDGE,"E60")])]})});
            chamfer(context, id + "F16", {"entities" : qUnion([Q0, Q1, Q2, Q3, Q4, Q5, Q6, Q7, Q8, Q9]), "width" : 0.5 * mm, "tangentPropagation" : true});
        }
        {
            var Q0;
            Q0=makeQuery(id+"F1.opExtrude","CAP_FACE",FACE,{"disambiguationData":[OSD([sQuery(id+"F0.wireOp",EDGE,"E0.bottom"),sQuery(id+"F0.wireOp",EDGE,"E0.top"),sQuery(id+"F0.wireOp",EDGE,"E0.left"),sQuery(id+"F0.wireOp",EDGE,"E0.right")])],"isStart":true});
            var sketch = newSketch(context, id + "F17", { "sketchPlane" : qUnion([Q0])});
            skLineSegment(sketch, "E72.0", {"start": v(195, 125) * mm, "end": v(195, -175) * mm, "construction": true});
            skLineSegment(sketch, "E73.0", {"start": v(-195, 325) * mm, "end": v(-195, -325) * mm, "construction": true});
            skLineSegment(sketch, "E74", {"start": v(195, -25) * mm, "end": v(-195, -25) * mm, "construction": true});
            skCircle(sketch, "E75.0", {"center": v(82, 75) * mm, "radius": 4.75 * mm, "construction": true});
            skCircle(sketch, "E76.0", {"center": v(82, -125) * mm, "radius": 4.75 * mm, "construction": true});
            skLineSegment(sketch, "E77", {"start": v(-195, -118) * mm, "end": v(-68, -118) * mm, "construction": true});
            skLineSegment(sketch, "E78", {"start": v(-68, -118) * mm, "end": v(-68, -18) * mm, "construction": true});
            skLineSegment(sketch, "E79", {"start": v(-68, -18) * mm, "end": v(82, -18) * mm, "construction": true});
            skLineSegment(sketch, "E80", {"start": v(82, -18) * mm, "end": v(82, -43) * mm, "construction": true});
            skCircle(sketch, "E81", {"center": v(-68, -18) * mm, "radius": 4.25 * mm});
            skCircle(sketch, "E82", {"center": v(-43, -18) * mm, "radius": 5 * mm});
            skCircle(sketch, "E83", {"center": v(82, -43) * mm, "radius": 4.25 * mm});
            skLineSegment(sketch, "E84", {"start": v(7, -18) * mm, "end": v(7, 30.22) * mm, "construction": true});
            skCircle(sketch, "E85.1.0.0", {"center": v(-18, -18) * mm, "radius": 4.25 * mm});
            skCircle(sketch, "E85.2.0.0", {"center": v(32, -18) * mm, "radius": 4.25 * mm});
            skLineSegment(sketch, "E85.direction1", {"start": v(-68, -18) * mm, "end": v(-18, -18) * mm, "construction": true});
            skCircle(sketch, "E86.MirrorC", {"center": v(82, -193) * mm, "radius": 4.25 * mm});
            skCircle(sketch, "E87.MirrorC", {"center": v(32, -218) * mm, "radius": 4.25 * mm});
            skCircle(sketch, "E88.MirrorC", {"center": v(-18, -218) * mm, "radius": 4.25 * mm});
            skCircle(sketch, "E89.MirrorC", {"center": v(-43, -218) * mm, "radius": 5 * mm, "construction": true});
            skCircle(sketch, "E90.MirrorC", {"center": v(-68, -218) * mm, "radius": 4.25 * mm});
            skCircle(sketch, "E91.MirrorC", {"center": v(57, -218) * mm, "radius": 5 * mm});
            skSolve(sketch);
        }
        {
            var Q0;
            Q0 = qSketchRegion(id + "F17", true);
            extrude(context, id + "F18", {"entities" : qUnion([Q0]), "operationType" : NewBodyOperationType.REMOVE, "oppositeDirection" : true, "depth" : 25 * mm, "offsetDistance" : 25 * mm});
        }
        {
            var Q0;
            Q0=makeQuery(id+"F18.boolean.opBoolean","COPY",FACE,{"derivedFrom":makeQuery(id+"F18.opExtrude","SWEPT_FACE",FACE,{"disambiguationData":[OSD([sQuery(id+"F17.wireOp",EDGE,"E81")])]})});
            var Q1;
            Q1=makeQuery(id+"F18.boolean.opBoolean","COPY",FACE,{"derivedFrom":makeQuery(id+"F18.opExtrude","SWEPT_FACE",FACE,{"disambiguationData":[OSD([sQuery(id+"F17.wireOp",EDGE,"E82")])]})});
            var Q2;
            Q2=makeQuery(id+"F18.boolean.opBoolean","COPY",FACE,{"derivedFrom":makeQuery(id+"F18.opExtrude","SWEPT_FACE",FACE,{"disambiguationData":[OSD([sQuery(id+"F17.wireOp",EDGE,"E85.2.0.0")])]})});
            var Q3;
            Q3=makeQuery(id+"F18.boolean.opBoolean","COPY",FACE,{"derivedFrom":makeQuery(id+"F18.opExtrude","SWEPT_FACE",FACE,{"disambiguationData":[OSD([sQuery(id+"F17.wireOp",EDGE,"E85.1.0.0")])]})});
            var Q4;
            Q4=makeQuery(id+"F18.boolean.opBoolean","COPY",FACE,{"derivedFrom":makeQuery(id+"F18.opExtrude","SWEPT_FACE",FACE,{"disambiguationData":[OSD([sQuery(id+"F17.wireOp",EDGE,"E83")])]})});
            var Q5;
            Q5=makeQuery(id+"F18.boolean.opBoolean","COPY",FACE,{"derivedFrom":makeQuery(id+"F18.opExtrude","SWEPT_FACE",FACE,{"disambiguationData":[OSD([sQuery(id+"F17.wireOp",EDGE,"E90.MirrorC")])]})});
            var Q6;
            Q6=makeQuery(id+"F18.boolean.opBoolean","COPY",FACE,{"derivedFrom":makeQuery(id+"F18.opExtrude","SWEPT_FACE",FACE,{"disambiguationData":[OSD([sQuery(id+"F17.wireOp",EDGE,"E88.MirrorC")])]})});
            var Q7;
            Q7=makeQuery(id+"F18.boolean.opBoolean","COPY",FACE,{"derivedFrom":makeQuery(id+"F18.opExtrude","SWEPT_FACE",FACE,{"disambiguationData":[OSD([sQuery(id+"F17.wireOp",EDGE,"E87.MirrorC")])]})});
            var Q8;
            Q8=makeQuery(id+"F18.boolean.opBoolean","COPY",FACE,{"derivedFrom":makeQuery(id+"F18.opExtrude","SWEPT_FACE",FACE,{"disambiguationData":[OSD([sQuery(id+"F17.wireOp",EDGE,"E91.MirrorC")])]})});
            var Q9;
            Q9=makeQuery(id+"F18.boolean.opBoolean","COPY",FACE,{"derivedFrom":makeQuery(id+"F18.opExtrude","SWEPT_FACE",FACE,{"disambiguationData":[OSD([sQuery(id+"F17.wireOp",EDGE,"E86.MirrorC")])]})});
            chamfer(context, id + "F19", {"entities" : qUnion([Q0, Q1, Q2, Q3, Q4, Q5, Q6, Q7, Q8, Q9]), "width" : 0.5 * mm, "tangentPropagation" : true});
        }
        {
            var Q0;
            Q0=makeQuery(id+"F1.opExtrude","CAP_FACE",FACE,{"disambiguationData":[OSD([sQuery(id+"F0.wireOp",EDGE,"E0.bottom"),sQuery(id+"F0.wireOp",EDGE,"E0.top"),sQuery(id+"F0.wireOp",EDGE,"E0.left"),sQuery(id+"F0.wireOp",EDGE,"E0.right")])],"isStart":false});
            var sketch = newSketch(context, id + "F20", { "sketchPlane" : qUnion([Q0])});
            skLineSegment(sketch, "E92.0", {"start": v(167.5, -125) * mm, "end": v(195, -125) * mm, "construction": true});
            skLineSegment(sketch, "E93.0", {"start": v(165, -127.5) * mm, "end": v(165, -325) * mm, "construction": true});
            skLineSegment(sketch, "E94", {"start": v(151, -145) * mm, "end": v(151, -205) * mm, "construction": true});
            skLineSegment(sketch, "E95.bottom", {"start": v(163, -130) * mm, "end": v(139, -130) * mm, "construction": true});
            skLineSegment(sketch, "E95.top", {"start": v(163, -220) * mm, "end": v(139, -220) * mm, "construction": true});
            skLineSegment(sketch, "E95.left", {"start": v(163, -130) * mm, "end": v(163, -220) * mm, "construction": true});
            skLineSegment(sketch, "E95.right", {"start": v(139, -130) * mm, "end": v(139, -220) * mm, "construction": true});
            skPoint(sketch, "E95.middle", {"position": v(151, -175) * mm});
            skCircle(sketch, "E96", {"center": v(151, -145) * mm, "radius": 5.5 * mm});
            skCircle(sketch, "E97", {"center": v(151, -145) * mm, "radius": 9 * mm});
            skCircle(sketch, "E98.0.1.0", {"center": v(151, -175) * mm, "radius": 5.5 * mm});
            skCircle(sketch, "E98.0.1.1", {"center": v(151, -175) * mm, "radius": 9 * mm});
            skCircle(sketch, "E98.0.2.0", {"center": v(151, -205) * mm, "radius": 5.5 * mm});
            skCircle(sketch, "E98.0.2.1", {"center": v(151, -205) * mm, "radius": 9 * mm});
            skLineSegment(sketch, "E98.direction1", {"start": v(151, -145) * mm, "end": v(176, -145) * mm, "construction": true});
            skLineSegment(sketch, "E98.direction2", {"start": v(151, -145) * mm, "end": v(151, -175) * mm, "construction": true});
            skSolve(sketch);
        }
        {
            var Q0;
            Q0=makeQuery(id+"F20.imprint","IMPRINT",FACE,{"disambiguationData":[TD([[makeQuery(id+"F20.imprint","IMPRINT",EDGE,{"derivedFrom":sQuery(id+"F20.wireOp",EDGE,"E96")}),1.0]])]});
            var Q1;
            Q1=makeQuery(id+"F20.imprint","IMPRINT",FACE,{"disambiguationData":[TD([[makeQuery(id+"F20.imprint","IMPRINT",EDGE,{"derivedFrom":sQuery(id+"F20.wireOp",EDGE,"E98.0.1.0")}),1.0]])]});
            var Q2;
            Q2=makeQuery(id+"F20.imprint","IMPRINT",FACE,{"disambiguationData":[TD([[makeQuery(id+"F20.imprint","IMPRINT",EDGE,{"derivedFrom":sQuery(id+"F20.wireOp",EDGE,"E98.0.2.0")}),1.0]])]});
            extrude(context, id + "F21", {"entities" : qUnion([Q0, Q1, Q2]), "operationType" : NewBodyOperationType.REMOVE, "oppositeDirection" : true, "depth" : 25 * mm, "offsetDistance" : 25 * mm});
        }
        {
            var Q0;
            Q0=makeQuery(id+"F20.imprint","IMPRINT",FACE,{"disambiguationData":[TD([[makeQuery(id+"F20.imprint","IMPRINT",EDGE,{"derivedFrom":sQuery(id+"F20.wireOp",EDGE,"E96")}),-1.0]])]});
            var Q1;
            Q1=makeQuery(id+"F20.imprint","IMPRINT",FACE,{"disambiguationData":[TD([[makeQuery(id+"F20.imprint","IMPRINT",EDGE,{"derivedFrom":sQuery(id+"F20.wireOp",EDGE,"E98.0.1.0")}),-1.0]])]});
            var Q2;
            Q2=makeQuery(id+"F20.imprint","IMPRINT",FACE,{"disambiguationData":[TD([[makeQuery(id+"F20.imprint","IMPRINT",EDGE,{"derivedFrom":sQuery(id+"F20.wireOp",EDGE,"E98.0.2.0")}),-1.0]])]});
            extrude(context, id + "F22", {"entities" : qUnion([Q0, Q1, Q2]), "operationType" : NewBodyOperationType.REMOVE, "oppositeDirection" : true, "depth" : 11 * mm, "offsetDistance" : 25 * mm});
        }
        {
            var Q0;
            Q0=makeQuery(id+"F22.boolean.opBoolean","COPY",EDGE,{"derivedFrom":makeQuery(id+"F22.opExtrude","CAP_EDGE",EDGE,{"disambiguationData":[OSD([sQuery(id+"F20.wireOp",EDGE,"E97")])],"isStart":true})});
            var Q1;
            Q1=makeQuery(id+"F22.boolean.opBoolean","COPY",EDGE,{"derivedFrom":makeQuery(id+"F22.opExtrude","CAP_EDGE",EDGE,{"disambiguationData":[OSD([sQuery(id+"F20.wireOp",EDGE,"E98.0.1.1")])],"isStart":true})});
            var Q2;
            Q2=makeQuery(id+"F22.boolean.opBoolean","COPY",EDGE,{"derivedFrom":makeQuery(id+"F22.opExtrude","CAP_EDGE",EDGE,{"disambiguationData":[OSD([sQuery(id+"F20.wireOp",EDGE,"E98.0.2.1")])],"isStart":true})});
            var Q3;
            Q3=makeQuery(id+"F21.boolean.opBoolean","INTERSECT",EDGE,{"derivedFrom":[makeQuery(id+"F1.opExtrude","CAP_FACE",FACE,{"disambiguationData":[OSD([sQuery(id+"F0.wireOp",EDGE,"E0.bottom"),sQuery(id+"F0.wireOp",EDGE,"E0.top"),sQuery(id+"F0.wireOp",EDGE,"E0.left"),sQuery(id+"F0.wireOp",EDGE,"E0.right")])],"isStart":true}),makeQuery(id+"F21.opExtrude","SWEPT_FACE",FACE,{"disambiguationData":[OSD([sQuery(id+"F20.wireOp",EDGE,"E98.0.2.0")])]})]});
            var Q4;
            Q4=makeQuery(id+"F21.boolean.opBoolean","INTERSECT",EDGE,{"derivedFrom":[makeQuery(id+"F1.opExtrude","CAP_FACE",FACE,{"disambiguationData":[OSD([sQuery(id+"F0.wireOp",EDGE,"E0.bottom"),sQuery(id+"F0.wireOp",EDGE,"E0.top"),sQuery(id+"F0.wireOp",EDGE,"E0.left"),sQuery(id+"F0.wireOp",EDGE,"E0.right")])],"isStart":true}),makeQuery(id+"F21.opExtrude","SWEPT_FACE",FACE,{"disambiguationData":[OSD([sQuery(id+"F20.wireOp",EDGE,"E98.0.1.0")])]})]});
            var Q5;
            Q5=makeQuery(id+"F21.boolean.opBoolean","INTERSECT",EDGE,{"derivedFrom":[makeQuery(id+"F1.opExtrude","CAP_FACE",FACE,{"disambiguationData":[OSD([sQuery(id+"F0.wireOp",EDGE,"E0.bottom"),sQuery(id+"F0.wireOp",EDGE,"E0.top"),sQuery(id+"F0.wireOp",EDGE,"E0.left"),sQuery(id+"F0.wireOp",EDGE,"E0.right")])],"isStart":true}),makeQuery(id+"F21.opExtrude","SWEPT_FACE",FACE,{"disambiguationData":[OSD([sQuery(id+"F20.wireOp",EDGE,"E96")])]})]});
            chamfer(context, id + "F23", {"entities" : qUnion([Q0, Q1, Q2, Q3, Q4, Q5]), "width" : 0.5 * mm, "tangentPropagation" : true});
        }
        {
            var Q0;
            Q0=makeQuery(id+"F1.opExtrude","CAP_FACE",FACE,{"disambiguationData":[OSD([sQuery(id+"F0.wireOp",EDGE,"E0.bottom"),sQuery(id+"F0.wireOp",EDGE,"E0.top"),sQuery(id+"F0.wireOp",EDGE,"E0.left"),sQuery(id+"F0.wireOp",EDGE,"E0.right")])],"isStart":false});
            var sketch = newSketch(context, id + "F24", { "sketchPlane" : qUnion([Q0])});
            skLineSegment(sketch, "E99.0", {"start": v(-195, -325) * mm, "end": v(165, -325) * mm, "construction": true});
            skLineSegment(sketch, "E100.0", {"start": v(-195, -325) * mm, "end": v(-195, 325) * mm, "construction": true});
            skLineSegment(sketch, "E101.bottom", {"start": v(20, -195) * mm, "end": v(80, -195) * mm, "construction": true});
            skLineSegment(sketch, "E101.top", {"start": v(20, -295) * mm, "end": v(80, -295) * mm, "construction": true});
            skLineSegment(sketch, "E101.left", {"start": v(20, -195) * mm, "end": v(20, -295) * mm, "construction": true});
            skLineSegment(sketch, "E101.right", {"start": v(80, -195) * mm, "end": v(80, -295) * mm, "construction": true});
            skCircle(sketch, "E102", {"center": v(20, -195) * mm, "radius": 2.5 * mm});
            skCircle(sketch, "E103", {"center": v(80, -195) * mm, "radius": 2.5 * mm});
            skCircle(sketch, "E104", {"center": v(80, -295) * mm, "radius": 2.5 * mm});
            skCircle(sketch, "E105", {"center": v(20, -295) * mm, "radius": 2.5 * mm});
            skSolve(sketch);
        }
        {
            var Q0;
            Q0=makeQuery(id+"F1.opExtrude","SWEPT_FACE",FACE,{"disambiguationData":[OSD([sQuery(id+"F0.wireOp",EDGE,"E0.bottom")])]});
            var sketch = newSketch(context, id + "F25", { "sketchPlane" : qUnion([Q0])});
            skLineSegment(sketch, "E106.0", {"start": v(-195, 24) * mm, "end": v(-195, 0) * mm, "construction": true});
            skLineSegment(sketch, "E107.0", {"start": v(-195, 24) * mm, "end": v(165, 24) * mm, "construction": true});
            skLineSegment(sketch, "E108", {"start": v(2.5, 9) * mm, "end": v(82.5, 9) * mm, "construction": true});
            skCircle(sketch, "E109", {"center": v(2.5, 9) * mm, "radius": 2.5 * mm});
            skCircle(sketch, "E110", {"center": v(82.5, 9) * mm, "radius": 2.5 * mm});
            skSolve(sketch);
        }
        {
            var Q0;
            Q0 = qSketchRegion(id + "F24", true);
            extrude(context, id + "F26", {"entities" : qUnion([Q0]), "operationType" : NewBodyOperationType.REMOVE, "oppositeDirection" : true, "depth" : 25 * mm, "offsetDistance" : 25 * mm});
        }
        {
            var Q0;
            Q0 = qSketchRegion(id + "F25", true);
            extrude(context, id + "F27", {"entities" : qUnion([Q0]), "operationType" : NewBodyOperationType.REMOVE, "oppositeDirection" : true, "depth" : 25 * mm, "offsetDistance" : 25 * mm});
        }
        {
            var Q0;
            Q0=makeQuery(id+"F27.boolean.opBoolean","COPY",FACE,{"derivedFrom":makeQuery(id+"F27.opExtrude","CAP_FACE",FACE,{"disambiguationData":[OSD([sQuery(id+"F25.wireOp",EDGE,"E109")])],"isStart":false})});
            var Q1;
            Q1=makeQuery(id+"F27.boolean.opBoolean","COPY",FACE,{"derivedFrom":makeQuery(id+"F27.opExtrude","CAP_FACE",FACE,{"disambiguationData":[OSD([sQuery(id+"F25.wireOp",EDGE,"E110")])],"isStart":false})});
            chamfer(context, id + "F28", {"entities" : qUnion([Q0, Q1]), "width" : 2.5 * mm, "tangentPropagation" : true});
        }
        {
            var Q0;
            Q0=makeQuery(id+"F27.boolean.opBoolean","COPY",EDGE,{"derivedFrom":makeQuery(id+"F27.opExtrude","CAP_EDGE",EDGE,{"disambiguationData":[OSD([sQuery(id+"F25.wireOp",EDGE,"E110")])],"isStart":true})});
            var Q1;
            Q1=makeQuery(id+"F27.boolean.opBoolean","COPY",EDGE,{"derivedFrom":makeQuery(id+"F27.opExtrude","CAP_EDGE",EDGE,{"disambiguationData":[OSD([sQuery(id+"F25.wireOp",EDGE,"E109")])],"isStart":true})});
            var Q2;
            Q2=makeQuery(id+"F26.boolean.opBoolean","COPY",FACE,{"derivedFrom":makeQuery(id+"F26.opExtrude","SWEPT_FACE",FACE,{"disambiguationData":[OSD([sQuery(id+"F24.wireOp",EDGE,"E105")])]})});
            var Q3;
            Q3=makeQuery(id+"F26.boolean.opBoolean","COPY",FACE,{"derivedFrom":makeQuery(id+"F26.opExtrude","SWEPT_FACE",FACE,{"disambiguationData":[OSD([sQuery(id+"F24.wireOp",EDGE,"E104")])]})});
            var Q4;
            Q4=makeQuery(id+"F26.boolean.opBoolean","COPY",FACE,{"derivedFrom":makeQuery(id+"F26.opExtrude","SWEPT_FACE",FACE,{"disambiguationData":[OSD([sQuery(id+"F24.wireOp",EDGE,"E102")])]})});
            var Q5;
            Q5=makeQuery(id+"F26.boolean.opBoolean","COPY",FACE,{"derivedFrom":makeQuery(id+"F26.opExtrude","SWEPT_FACE",FACE,{"disambiguationData":[OSD([sQuery(id+"F24.wireOp",EDGE,"E103")])]})});
            chamfer(context, id + "F29", {"entities" : qUnion([Q0, Q1, Q2, Q3, Q4, Q5]), "width" : 0.5 * mm, "tangentPropagation" : true});
        }
    });
